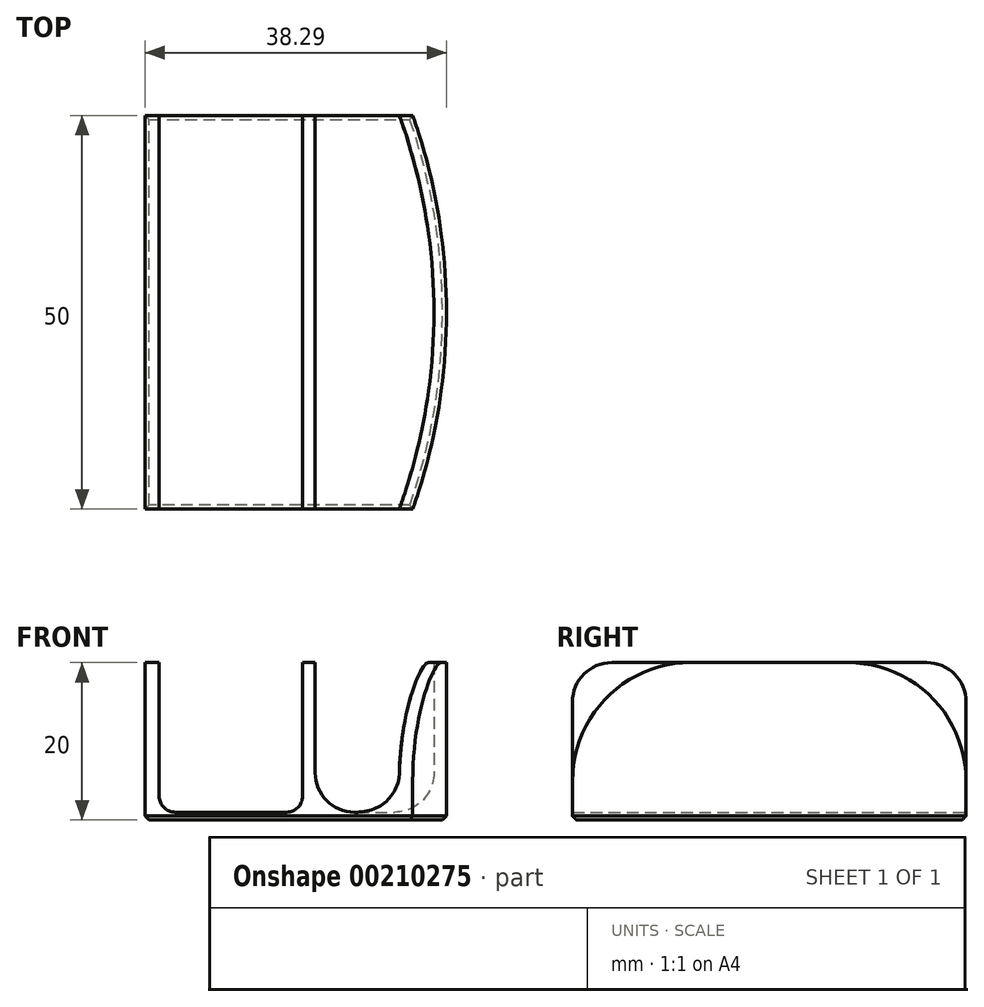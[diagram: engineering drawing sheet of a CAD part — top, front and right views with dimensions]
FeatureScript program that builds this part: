
annotation { "Feature Type Name" : "Feature", "Feature Type Description" : "" }
export const myFeature = defineFeature(function(context is Context, id is Id, definition is map)
    precondition{}
    {
        {
            var Q0;
            Q0=qCreatedBy(makeId("Top.planeOp"),FACE);
            var sketch = newSketch(context, id + "F0", { "sketchPlane" : qUnion([Q0])});
            skLineSegment(sketch, "E0.bottom", {"start": v(0, 0) * mm, "end": v(34, 0) * mm});
            skLineSegment(sketch, "E0.top", {"start": v(0, 50) * mm, "end": v(34, 50) * mm});
            skLineSegment(sketch, "E0.left", {"start": v(0, 0) * mm, "end": v(0, 50) * mm});
            skLineSegment(sketch, "E1", {"start": v(1.8, 50) * mm, "end": v(1.8, 0) * mm});
            skArc(sketch, "E2", {"start": v(34, 0) * mm, "mid": v(38.29, 25) * mm, "end": v(34, 50) * mm});
            skArc(sketch, "E3.0", {"start": v(32.3, 0) * mm, "mid": v(36.69, 25) * mm, "end": v(32.3, 50) * mm});
            skLineSegment(sketch, "E4", {"start": v(20, 50) * mm, "end": v(20, 0) * mm});
            skLineSegment(sketch, "E5", {"start": v(21.6, 50) * mm, "end": v(21.6, 0) * mm});
            skSolve(sketch);
        }
        {
            var Q0;
            Q0=qSketchRegion(id+"F0",true);
            extrude(context, id + "F1", {"entities" : qUnion([Q0]), "depth" : 1 * mm});
        }
        {
            var Q0;
            {var subQ1=sQuery(id+"F0.wireOp",EDGE,"E0.left");Q0=makeQuery(id+"F0.imprint","IMPRINT",FACE,{"disambiguationData":[TD([[makeQuery(id+"F0.imprint","IMPRINT",EDGE,{"derivedFrom":subQ1}),-1.0]])]});}
            var Q1;
            {var subQ1=sQuery(id+"F0.wireOp",EDGE,"E4");Q1=makeQuery(id+"F0.imprint","IMPRINT",FACE,{"disambiguationData":[TD([[makeQuery(id+"F0.imprint","IMPRINT",EDGE,{"derivedFrom":subQ1}),1.0]])]});}
            extrude(context, id + "F2", {"entities" : qUnion([Q0, Q1]), "operationType" : NewBodyOperationType.ADD, "depth" : 20 * mm});
        }
        {
            var Q0;
            {var subQ1=sQuery(id+"F0.wireOp",EDGE,"E2");Q0=makeQuery(id+"F0.imprint","IMPRINT",FACE,{"disambiguationData":[TD([[makeQuery(id+"F0.imprint","IMPRINT",EDGE,{"derivedFrom":subQ1}),1.0]])]});}
            extrude(context, id + "F3", {"entities" : qUnion([Q0]), "operationType" : NewBodyOperationType.ADD, "depth" : 20 * mm});
        }
        {
            var Q0;
            Q0=makeQuery(id+"F3.opExtrude","CAP_EDGE",EDGE,{"disambiguationData":[OSD([sQuery(id+"F0.wireOp",EDGE,"E0.bottom")])],"isStart":false});
            var Q1;
            Q1=makeQuery(id+"F3.opExtrude","CAP_EDGE",EDGE,{"disambiguationData":[OSD([sQuery(id+"F0.wireOp",EDGE,"E0.top")])],"isStart":false});
            fillet(context, id + "F4", {"entities" : qUnion([Q0, Q1]), "radius" : 15 * mm, "tangentPropagation" : true, "allowEdgeOverflow" : false});
        }
        {
            var Q0;
            {var subQ0=sQuery(id+"F0.wireOp",EDGE,"E0.bottom");var subQ1=sQuery(id+"F0.wireOp",EDGE,"E0.top");var subQ2=sQuery(id+"F0.wireOp",EDGE,"E0.left");var subQ3=sQuery(id+"F0.wireOp",EDGE,"E2");Q0=makeQuery(id+"F3.boolean.opBoolean","INTERSECT",EDGE,{"derivedFrom":[makeQuery(id+"F2.boolean.opBoolean","SPLIT",FACE,{"disambiguationData":[TD([makeQuery(id+"F1.opExtrude","SWEPT_FACE",FACE,{"disambiguationData":[OSD([subQ3])]})])],"derivedFrom":makeQuery(id+"F1.opExtrude","CAP_FACE",FACE,{"disambiguationData":[OSD([subQ0,subQ1,subQ2,subQ3])],"isStart":false})}),makeQuery(id+"F3.opExtrude","SWEPT_FACE",FACE,{"disambiguationData":[OSD([sQuery(id+"F0.wireOp",EDGE,"E3.0")])]})]});}
            var Q1;
            Q1=makeQuery(id+"F2.boolean.opBoolean","INTERSECT",EDGE,{"derivedFrom":[makeQuery(id+"F1.opExtrude","CAP_FACE",FACE,{"disambiguationData":[OSD([sQuery(id+"F0.wireOp",EDGE,"E0.bottom"),sQuery(id+"F0.wireOp",EDGE,"E0.top"),sQuery(id+"F0.wireOp",EDGE,"E0.left"),sQuery(id+"F0.wireOp",EDGE,"E2")])],"isStart":false}),makeQuery(id+"F2.opExtrude","SWEPT_FACE",FACE,{"disambiguationData":[OSD([sQuery(id+"F0.wireOp",EDGE,"E5")])]})]});
            fillet(context, id + "F5", {"entities" : qUnion([Q0, Q1]), "radius" : 5 * mm, "tangentPropagation" : true, "allowEdgeOverflow" : false});
        }
        {
            var Q0;
            Q0=makeQuery(id+"F2.boolean.opBoolean","INTERSECT",EDGE,{"derivedFrom":[makeQuery(id+"F1.opExtrude","CAP_FACE",FACE,{"disambiguationData":[OSD([sQuery(id+"F0.wireOp",EDGE,"E0.bottom"),sQuery(id+"F0.wireOp",EDGE,"E0.top"),sQuery(id+"F0.wireOp",EDGE,"E0.left"),sQuery(id+"F0.wireOp",EDGE,"E2")])],"isStart":false}),makeQuery(id+"F2.opExtrude","SWEPT_FACE",FACE,{"disambiguationData":[OSD([sQuery(id+"F0.wireOp",EDGE,"E1")])]})]});
            var Q1;
            Q1=makeQuery(id+"F2.boolean.opBoolean","INTERSECT",EDGE,{"derivedFrom":[makeQuery(id+"F1.opExtrude","CAP_FACE",FACE,{"disambiguationData":[OSD([sQuery(id+"F0.wireOp",EDGE,"E0.bottom"),sQuery(id+"F0.wireOp",EDGE,"E0.top"),sQuery(id+"F0.wireOp",EDGE,"E0.left"),sQuery(id+"F0.wireOp",EDGE,"E2")])],"isStart":false}),makeQuery(id+"F2.opExtrude","SWEPT_FACE",FACE,{"disambiguationData":[OSD([sQuery(id+"F0.wireOp",EDGE,"E4")])]})]});
            fillet(context, id + "F6", {"entities" : qUnion([Q0, Q1]), "radius" : 2 * mm, "tangentPropagation" : true, "allowEdgeOverflow" : false});
        }
        {
            var Q0;
            {var subQ0=sQuery(id+"F0.wireOp",EDGE,"E0.bottom");Q0=makeQuery(id+"F2.opExtrude","CAP_EDGE",EDGE,{"disambiguationData":[OSD([subQ0]),TDD([makeQuery(id+"F0.imprint","IMPRINT",EDGE,{"disambiguationData":[TD([[makeQuery(id+"F0.imprint","INTERSECT",VERTEX,{"derivedFrom":[subQ0,sQuery(id+"F0.wireOp",EDGE,"E0.left")]}),-1.0]])],"derivedFrom":subQ0})])],"isStart":false});}
            var Q1;
            {var subQ0=sQuery(id+"F0.wireOp",EDGE,"E0.bottom");Q1=makeQuery(id+"F2.opExtrude","CAP_EDGE",EDGE,{"disambiguationData":[OSD([subQ0]),TDD([makeQuery(id+"F0.imprint","IMPRINT",EDGE,{"disambiguationData":[TD([[makeQuery(id+"F0.imprint","INTERSECT",VERTEX,{"derivedFrom":[subQ0,sQuery(id+"F0.wireOp",EDGE,"E4")]}),-1.0]])],"derivedFrom":subQ0})])],"isStart":false});}
            var Q2;
            {var subQ0=sQuery(id+"F0.wireOp",EDGE,"E0.top");Q2=makeQuery(id+"F2.opExtrude","CAP_EDGE",EDGE,{"disambiguationData":[OSD([subQ0]),TDD([makeQuery(id+"F0.imprint","IMPRINT",EDGE,{"disambiguationData":[TD([[makeQuery(id+"F0.imprint","INTERSECT",VERTEX,{"derivedFrom":[subQ0,sQuery(id+"F0.wireOp",EDGE,"E4")]}),-1.0]])],"derivedFrom":subQ0})])],"isStart":false});}
            var Q3;
            {var subQ0=sQuery(id+"F0.wireOp",EDGE,"E0.top");Q3=makeQuery(id+"F2.opExtrude","CAP_EDGE",EDGE,{"disambiguationData":[OSD([subQ0]),TDD([makeQuery(id+"F0.imprint","IMPRINT",EDGE,{"disambiguationData":[TD([[makeQuery(id+"F0.imprint","INTERSECT",VERTEX,{"derivedFrom":[subQ0,sQuery(id+"F0.wireOp",EDGE,"E0.left")]}),-1.0]])],"derivedFrom":subQ0})])],"isStart":false});}
            fillet(context, id + "F7", {"entities" : qUnion([Q0, Q1, Q2, Q3]), "radius" : 5 * mm, "tangentPropagation" : true, "allowEdgeOverflow" : false});
        }
        {
            var Q0;
            Q0=makeQuery(id+"F1.opExtrude","CAP_FACE",FACE,{"disambiguationData":[OSD([sQuery(id+"F0.wireOp",EDGE,"E0.bottom"),sQuery(id+"F0.wireOp",EDGE,"E0.top"),sQuery(id+"F0.wireOp",EDGE,"E0.left"),sQuery(id+"F0.wireOp",EDGE,"E2")])],"isStart":true});
            chamfer(context, id + "F8", {"entities" : qUnion([Q0]), "width" : .5 * mm, "tangentPropagation" : true});
        }
    });
